# Revit family: Door-2-Panel
name_source: partatom
category: Doors
units: mm (PartAtom-declared; Revit-internal decimal feet)

## family parameters
Always vertical = Yes
Classification Number = 23.30.10.11.17
Cut with Voids When Loaded = No
Host = Wall
Room Calculation Point = No
Shared = No

## types (36) — shared parameters
Assembly Code = C1020100
Building Codes = http://www.iccsafe.org
CasingMaterial = ARCAT - Wood - Pine_Northern White
CladdingMaterial = ARCAT - Metal - Aluminum_0.032" - Burgundy
Construction Details = http://www.arcat.com
ENERGYSTAR Rating = North/Central
Expected Lifespan (Years) = 15
Fax = (203) 929-2444
Function = Interior
Glass Thickness = 0' - 0 11/32"
Glass Type = ARCAT - Glass - Tempered - Clear
Green Building-LEED = http://www.arcat.com
HandleHeight = 3' - 0"
Hardware Backset = 0' - 2 3/8"
JambMaterial = ARCAT - Wood - Pine_Northern White
JambThickness = 0' - 0 3/4"
Keynote = 08200
LateralClearance = 0' - 1 1/2"
Maintenance Schedule (Months) = 36
Manufacturer = Generic
Model = Generic
Panel Type = Door-2-Panel : ByType
Product Data = http://www.arcat.com
Product Properties = http://www.arcat.com
Rail-Bottom = 1' - 0"
Rail-Top = 0' - 8"
Rough Opening Clearance = 0' - 0 3/4"
SHGC = 0.54
SlabThickness = 0' - 1 3/8"
Specification = http://www.arcat.com
Test Data = http://www.aamanet.org
Thickness = 0' - 1 3/8"
URL = http://www.arcat.com
U_Factor = 0.39
Usage = Interior
Wall Closure = By host
Warranty Duration (Years) = 10
zero-valued in all types: R_Value

## per-type parameters (varying)
| type | Description | Fire Rating | Height | Rough Height | Rough Width | SlabMaterial | Width |
| 3-0 x 8-0 Steel | 3-0 x 8-0 Raised 2 Panel Steel Door | 90 Minute | 8' - 0" | 8' - 1 1/2" | 3' - 3" | ARCAT - Metal - Steel 18ga - Mill | 3' - 0" |
| 2-8 x 8-0 Steel | 2-8 x 8-0 Raised 2 Panel Steel Door | 90 Minute | 8' - 0" | 8' - 1 1/2" | 2' - 11" | ARCAT - Metal - Steel 18ga - Mill | 2' - 8" |
| 2-6 x 8-0 Steel | 2-6 x 8-0 Raised 2 Panel Steel Door | 90 Minute | 8' - 0" | 8' - 1 1/2" | 2' - 9" | ARCAT - Metal - Steel 18ga - Mill | 2' - 6" |
| 2-4 x 8-0 Steel | 2-4 x 8-0 Raised 2 Panel Steel Door | 90 Minute | 8' - 0" | 8' - 1 1/2" | 2' - 7" | ARCAT - Metal - Steel 18ga - Mill | 2' - 4" |
| 2-0 x 8-0 Steel | 2-0 x 8-0 Raised 2 Panel Steel Door | 90 Minute | 8' - 0" | 8' - 1 1/2" | 2' - 3" | ARCAT - Metal - Steel 18ga - Mill | 2' - 0" |
| 1-8 x 8-0 Steel | 1-8 x 8-0 Raised 2 Panel Steel Door | 90 Minute | 8' - 0" | 8' - 1 1/2" | 1' - 11" | ARCAT - Metal - Steel 18ga - Mill | 1' - 8" |
| 3-0 x 7-6 Steel | 3-0 x 7-6 Raised 2 Panel Steel Door | 90 Minute | 7' - 6" | 7' - 7 1/2" | 3' - 3" | ARCAT - Metal - Steel 18ga - Mill | 3' - 0" |
| 2-8 x 7-6 Steel | 2-8 x 7-6 Raised 2 Panel Steel Door | 90 Minute | 7' - 6" | 7' - 7 1/2" | 2' - 11" | ARCAT - Metal - Steel 18ga - Mill | 2' - 8" |
| 2-6 x 7-6 Steel | 2-6 x 7-6 Raised 2 Panel Steel Door | 90 Minute | 7' - 6" | 7' - 7 1/2" | 2' - 9" | ARCAT - Metal - Steel 18ga - Mill | 2' - 6" |
| 2-4 x 7-6 Steel | 2-4 x 7-6 Raised 2 Panel Steel Door | 90 Minute | 7' - 6" | 7' - 7 1/2" | 2' - 7" | ARCAT - Metal - Steel 18ga - Mill | 2' - 4" |
| 2-0 x 7-6 Steel | 2-0 x 7-6 Raised 2 Panel Steel Door | 90 Minute | 7' - 6" | 7' - 7 1/2" | 2' - 3" | ARCAT - Metal - Steel 18ga - Mill | 2' - 0" |
| 1-8 x 7-6 Steel | 1-8 x 7-6 Raised 2 Panel Steel Door | 90 Minute | 7' - 6" | 7' - 7 1/2" | 1' - 11" | ARCAT - Metal - Steel 18ga - Mill | 1' - 8" |
| 3-0 x 6-8 Steel | 3-0 x 6-8 Raised 2 Panel Steel Door | 90 Minute | 6' - 8" | 6' - 9 1/2" | 3' - 3" | ARCAT - Metal - Steel 18ga - Mill | 3' - 0" |
| 2-8 x 6-8 Steel | 2-8 x 6-8 Raised 2 Panel Steel Door | 90 Minute | 6' - 8" | 6' - 9 1/2" | 2' - 11" | ARCAT - Metal - Steel 18ga - Mill | 2' - 8" |
| 2-6 x 6-8 Steel | 2-6 x 6-8 Raised 2 Panel Steel Door | 90 Minute | 6' - 8" | 6' - 9 1/2" | 2' - 9" | ARCAT - Metal - Steel 18ga - Mill | 2' - 6" |
| 2-4 x 6-8 Steel | 2-4 x 6-8 Raised 2 Panel Steel Door | 90 Minute | 6' - 8" | 6' - 9 1/2" | 2' - 7" | ARCAT - Metal - Steel 18ga - Mill | 2' - 4" |
| 2-0 x 6-8 Steel | 2-0 x 6-8 Raised 2 Panel Steel Door | 90 Minute | 6' - 8" | 6' - 9 1/2" | 2' - 3" | ARCAT - Metal - Steel 18ga - Mill | 2' - 0" |
| 1-8 x 6-8 Steel | 1-8 x 6-8 Raised 2 Panel Steel Door | 90 Minute | 6' - 8" | 6' - 9 1/2" | 1' - 11" | ARCAT - Metal - Steel 18ga - Mill | 1' - 8" |
| 3-0 x 8-0 Wood | 3-0 x 8-0 Raised 2 Panel Wood Door | 30 Minute | 8' - 0" | 8' - 1 1/2" | 3' - 3" | ARCAT - Wood - Pine_Northern White | 3' - 0" |
| 2-8 x 8-0 Wood | 2-8 x 8-0 Raised 2 Panel Wood Door | 30 Minute | 8' - 0" | 8' - 1 1/2" | 2' - 11" | ARCAT - Wood - Pine_Northern White | 2' - 8" |
| 2-6 x 8-0 Wood | 2-6 x 8-0 Raised 2 Panel Wood Door | 30 Minute | 8' - 0" | 8' - 1 1/2" | 2' - 9" | ARCAT - Wood - Pine_Northern White | 2' - 6" |
| 2-4 x 8-0 Wood | 2-4 x 8-0 Raised 2 Panel Wood Door | 30 Minute | 8' - 0" | 8' - 1 1/2" | 2' - 7" | ARCAT - Wood - Pine_Northern White | 2' - 4" |
| 2-0 x 8-0 Wood | 2-0 x 8-0 Raised 2 Panel Wood Door | 30 Minute | 8' - 0" | 8' - 1 1/2" | 2' - 3" | ARCAT - Wood - Pine_Northern White | 2' - 0" |
| 1-8 x 8-0 Wood | 1-8 x 8-0 Raised 2 Panel Wood Door | 30 Minute | 8' - 0" | 8' - 1 1/2" | 1' - 11" | ARCAT - Wood - Pine_Northern White | 1' - 8" |
| 3-0 x 7-6 Wood | 3-0 x 7-6 Raised 2 Panel Wood Door | 30 Minute | 7' - 6" | 7' - 7 1/2" | 3' - 3" | ARCAT - Wood - Pine_Northern White | 3' - 0" |
| 2-8 x 7-6 Wood | 2-8 x 7-6 Raised 2 Panel Wood Door | 30 Minute | 7' - 6" | 7' - 7 1/2" | 2' - 11" | ARCAT - Wood - Pine_Northern White | 2' - 8" |
| 2-6 x 7-6 Wood | 2-6 x 7-6 Raised 2 Panel Wood Door | 30 Minute | 7' - 6" | 7' - 7 1/2" | 2' - 9" | ARCAT - Wood - Pine_Northern White | 2' - 6" |
| 2-4 x 7-6 Wood | 2-4 x 7-6 Raised 2 Panel Wood Door | 30 Minute | 7' - 6" | 7' - 7 1/2" | 2' - 7" | ARCAT - Wood - Pine_Northern White | 2' - 4" |
| 2-0 x 7-6 Wood | 2-0 x 7-6 Raised 2 Panel Wood Door | 30 Minute | 7' - 6" | 7' - 7 1/2" | 2' - 3" | ARCAT - Wood - Pine_Northern White | 2' - 0" |
| 1-8 x 7-6 Wood | 1-8 x 7-6 Raised 2 Panel Wood Door | 30 Minute | 7' - 6" | 7' - 7 1/2" | 1' - 11" | ARCAT - Wood - Pine_Northern White | 1' - 8" |
| 3-0 x 6-8 Wood | 3-0 x 6-8 Raised 2 Panel Wood Door | 30 Minute | 6' - 8" | 6' - 9 1/2" | 3' - 3" | ARCAT - Wood - Pine_Northern White | 3' - 0" |
| 2-8 x 6-8 Wood | 2-8 x 6-8 Raised 2 Panel Wood Door | 30 Minute | 6' - 8" | 6' - 9 1/2" | 2' - 11" | ARCAT - Wood - Pine_Northern White | 2' - 8" |
| 2-6 x 6-8 Wood | 2-6 x 6-8 Raised 2 Panel Wood Door | 30 Minute | 6' - 8" | 6' - 9 1/2" | 2' - 9" | ARCAT - Wood - Pine_Northern White | 2' - 6" |
| 2-4 x 6-8 Wood | 2-4 x 6-8 Raised 2 Panel Wood Door | 30 Minute | 6' - 8" | 6' - 9 1/2" | 2' - 7" | ARCAT - Wood - Pine_Northern White | 2' - 4" |
| 2-0 x 6-8 Wood | 2-0 x 6-8 Raised 2 Panel Wood Door | 30 Minute | 6' - 8" | 6' - 9 1/2" | 2' - 3" | ARCAT - Wood - Pine_Northern White | 2' - 0" |
| 1-8 x 6-8 Wood | 1-8 x 6-8 Raised 2 Panel Wood Door | 30 Minute | 6' - 8" | 6' - 9 1/2" | 1' - 11" | ARCAT - Wood - Pine_Northern White | 1' - 8" |

## geometry (parser evidence)
native form markers: Blend x1, Sweep x9
no freeform markers — native parametric forms only
